# Revit family: Kitchen_Sinks_hansgrohe_43436XXX-S51-S510-U760-Under-mount-sink_89765
name_source: partatom
category: Plumbing Fixtures
revit_build: Autodesk Revit 2018 (Build: 20170223_1515(x64)
units: mm (PartAtom-declared; Revit-internal decimal feet)

## family parameters
Cut with Voids When Loaded = No
Host = Face
OmniClass Number = 23.31.13.00
OmniClass Title = Sinks
Part Type = Normal
Room Calculation Point = No
Round Connector Dimension = Use Diameter
Shared = No

## types (3) — shared parameters
BIMobject category = Sinks
Connector Description = Water Outlet 45 mm
Default Elevation = 1219 mm
Description = S51 S510-U760 Under-mount sink 305/435
Design country = Germany
Diameter = 45  [stored 0.147638 ft]
Edition number = 1
IFC Classification = Sanitary Terminal
Manufacturer = Hansgrohe
Manufacturer country = Germany
Manufacturer name = hansgrohe
Material main = Natural Acrylic Stone
Model = 43436XXX
OmniClass Code = 23-31 13 00
OmniClass Description = Sinks
Product Guid = bf04fef4-9d0a-4764-bfc8-3be03146c347
Product SKU = 43436XXX
Product data url = https://bimobject.com
Product family = S51
Product group = Sinks
Product name = 43436XXX S51 S510-U760 Under-mount sink 305/435
Product url = https://www.hansgrohe.com
QR code = https://bimobject.com
UNSPSC Code = 30181504
URL = https://www.hansgrohe.com
Uniclass 2015 Code = Pr_40_20_96_45
Uniclass 2015 Name = Kitchen sinks
Weight Net (Kg) = 13.9

## per-type parameters (varying)
| type | Material |
| 170 Graphiteblack | Hansgrohe - Metal - 170 Graphiteblack |
| 290 Stonegrey | Hansgrohe - Metal - 290 Stonegrey |
| 380 Concretegrey | Hansgrohe - Metal - 380 Concretegrey |

note: [stored X ft] marks values corroborated as IEEE doubles in the binary element streams (Revit-internal decimal feet)

## geometry (parser evidence)
native form markers: Sweep x4
no freeform markers — native parametric forms only
